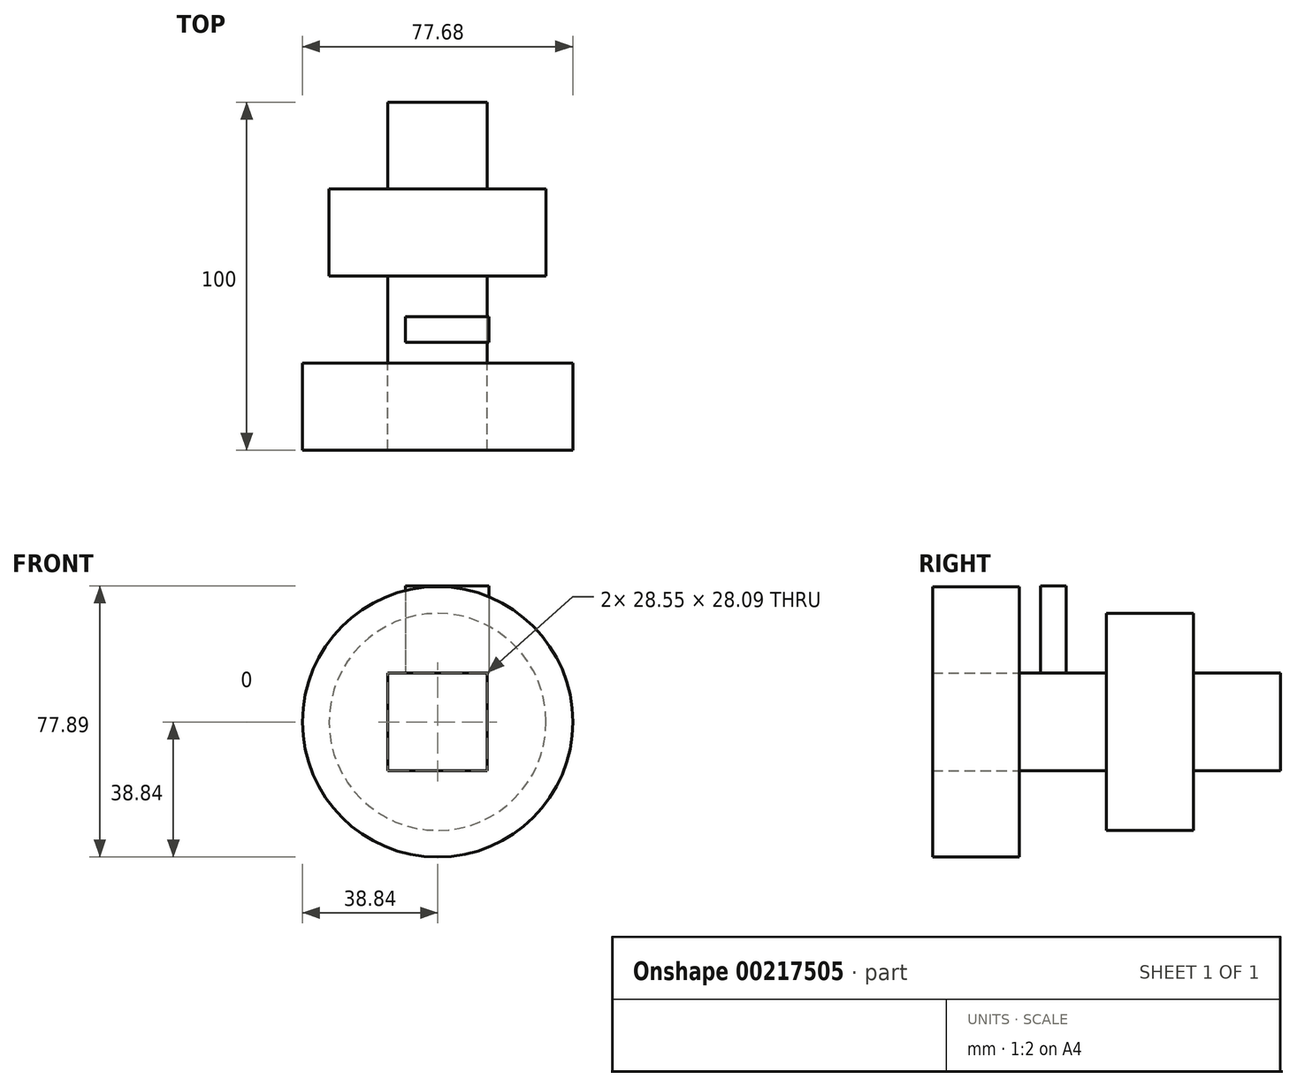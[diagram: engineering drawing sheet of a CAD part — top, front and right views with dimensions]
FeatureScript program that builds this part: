
annotation { "Feature Type Name" : "Feature", "Feature Type Description" : "" }
export const myFeature = defineFeature(function(context is Context, id is Id, definition is map)
    precondition{}
    {
        {
            var Q0;
            Q0=qCreatedBy(makeId("Front.planeOp"),FACE);
            var sketch = newSketch(context, id + "F0", { "sketchPlane" : qUnion([Q0])});
            skCircle(sketch, "E0", {"center": v(0, 0) * mm, "radius": 31.18 * mm});
            skSolve(sketch);
        }
        {
            var Q0;
            Q0=makeQuery(id+"F0.imprint","IMPRINT",FACE,{"disambiguationData":[TD([[makeQuery(id+"F0.imprint","IMPRINT",EDGE,{"derivedFrom":sQuery(id+"F0.wireOp",EDGE,"E0")}),1.0]])]});
            extrude(context, id + "F1", {"entities" : qUnion([Q0]), "oppositeDirection" : true, "depth" : 25 * mm});
        }
        {
            var Q0;
            Q0=makeQuery(id+"F1.opExtrude","CAP_FACE",FACE,{"disambiguationData":[OSD([sQuery(id+"F0.wireOp",EDGE,"E0")])],"isStart":true});
            var sketch = newSketch(context, id + "F2", { "sketchPlane" : qUnion([Q0])});
            skLineSegment(sketch, "E1.bottom", {"start": v(14.28, 14.05) * mm, "end": v(-14.28, 14.05) * mm});
            skLineSegment(sketch, "E1.top", {"start": v(14.28, -14.05) * mm, "end": v(-14.28, -14.05) * mm});
            skLineSegment(sketch, "E1.left", {"start": v(14.28, 14.05) * mm, "end": v(14.28, -14.05) * mm});
            skLineSegment(sketch, "E1.right", {"start": v(-14.28, 14.05) * mm, "end": v(-14.28, -14.05) * mm});
            skPoint(sketch, "E1.middle", {"position": v(0, 0) * mm});
            skSolve(sketch);
        }
        {
            var Q0;
            Q0 = qSketchRegion(id + "F2", true);
            extrude(context, id + "F3", {"entities" : qUnion([Q0]), "operationType" : NewBodyOperationType.ADD, "depth" : 25 * mm, "hasSecondDirection" : true, "secondDirectionOppositeDirection" : true, "secondDirectionDepth" : 50 * mm});
        }
        {
            var Q0;
            {var subQ2=sQuery(id+"F2.wireOp",EDGE,"E1.bottom");Q0=makeQuery(id+"F3.boolean.opBoolean","SPLIT",FACE,{"disambiguationData":[TD([makeQuery(id+"F1.opExtrude","CAP_FACE",FACE,{"disambiguationData":[OSD([sQuery(id+"F0.wireOp",EDGE,"E0")])],"isStart":true})])],"derivedFrom":makeQuery(id+"F3.opExtrude","SWEPT_FACE",FACE,{"disambiguationData":[OSD([subQ2])]})});}
            var sketch = newSketch(context, id + "F4", { "sketchPlane" : qUnion([Q0])});
            skLineSegment(sketch, "E2.bottom", {"start": v(-9.28, -11.62) * mm, "end": v(14.7, -11.62) * mm});
            skLineSegment(sketch, "E2.top", {"start": v(-9.28, -19.03) * mm, "end": v(14.7, -19.03) * mm});
            skLineSegment(sketch, "E2.left", {"start": v(-9.28, -11.62) * mm, "end": v(-9.28, -19.03) * mm});
            skLineSegment(sketch, "E2.right", {"start": v(14.7, -11.62) * mm, "end": v(14.7, -19.03) * mm});
            skSolve(sketch);
        }
        {
            var Q0;
            Q0 = qSketchRegion(id + "F4", true);
            extrude(context, id + "F5", {"entities" : qUnion([Q0]), "depth" : 25 * mm});
        }
        {
            var Q0;
            Q0=makeQuery(id+"F3.opExtrude","CAP_FACE",FACE,{"disambiguationData":[OSD([sQuery(id+"F2.wireOp",EDGE,"E1.bottom"),sQuery(id+"F2.wireOp",EDGE,"E1.top"),sQuery(id+"F2.wireOp",EDGE,"E1.left"),sQuery(id+"F2.wireOp",EDGE,"E1.right")])],"isStart":false});
            var sketch = newSketch(context, id + "F6", { "sketchPlane" : qUnion([Q0])});
            skCircle(sketch, "E3", {"center": v(0, 0) * mm, "radius": 38.84 * mm});
            skSolve(sketch);
        }
        {
            var Q0;
            Q0=makeQuery(id+"F6.imprint","IMPRINT",FACE,{"disambiguationData":[TD([[makeQuery(id+"F6.imprint","IMPRINT",EDGE,{"derivedFrom":sQuery(id+"F6.wireOp",EDGE,"E3")}),1.0]])]});
            extrude(context, id + "F7", {"entities" : qUnion([Q0]), "depth" : 25 * mm});
        }
    });
